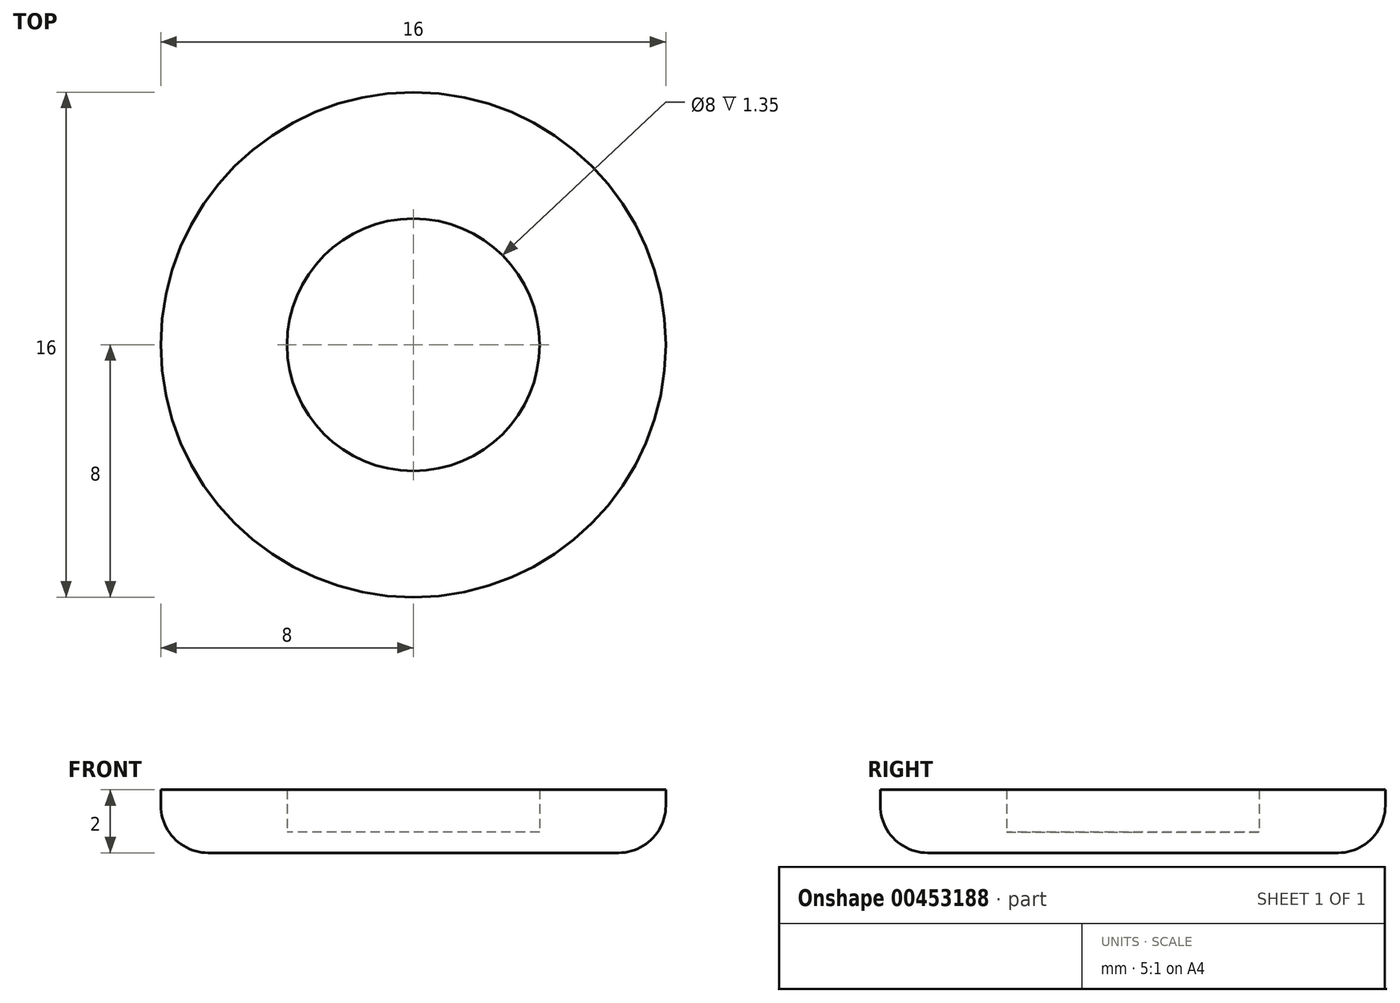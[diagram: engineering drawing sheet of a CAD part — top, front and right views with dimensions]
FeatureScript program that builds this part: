
annotation { "Feature Type Name" : "Feature", "Feature Type Description" : "" }
export const myFeature = defineFeature(function(context is Context, id is Id, definition is map)
    precondition{}
    {
        {
            var Q0;
            Q0=qCreatedBy(makeId("Top.planeOp"),FACE);
            var sketch = newSketch(context, id + "F0", { "sketchPlane" : qUnion([Q0])});
            skCircle(sketch, "E0", {"center": v(0, 0) * mm, "radius": 4 * mm});
            skCircle(sketch, "E1", {"center": v(0, 0) * mm, "radius": 8 * mm});
            skSolve(sketch);
        }
        {
            var Q0;
            Q0=makeQuery(id+"F0.imprint","IMPRINT",FACE,{"disambiguationData":[TD([[makeQuery(id+"F0.imprint","IMPRINT",EDGE,{"derivedFrom":sQuery(id+"F0.wireOp",EDGE,"E0")}),-1.0]])]});
            extrude(context, id + "F1", {"entities" : qUnion([Q0]), "depth" : 2 * mm});
        }
        {
            var Q0;
            Q0=makeQuery(id+"F0.imprint","IMPRINT",FACE,{"disambiguationData":[TD([[makeQuery(id+"F0.imprint","IMPRINT",EDGE,{"derivedFrom":sQuery(id+"F0.wireOp",EDGE,"E0")}),1.0]])]});
            extrude(context, id + "F2", {"entities" : qUnion([Q0]), "operationType" : NewBodyOperationType.ADD, "depth" : ((1.1 / 2) + .1) * mm});
        }
        {
            var Q0;
            Q0=makeQuery(id+"F1.opExtrude","CAP_EDGE",EDGE,{"disambiguationData":[OSD([sQuery(id+"F0.wireOp",EDGE,"E1")])],"isStart":true});
            fillet(context, id + "F3", {"entities" : qUnion([Q0]), "radius" : 1.5 * mm, "tangentPropagation" : true, "allowEdgeOverflow" : false});
        }
    });
